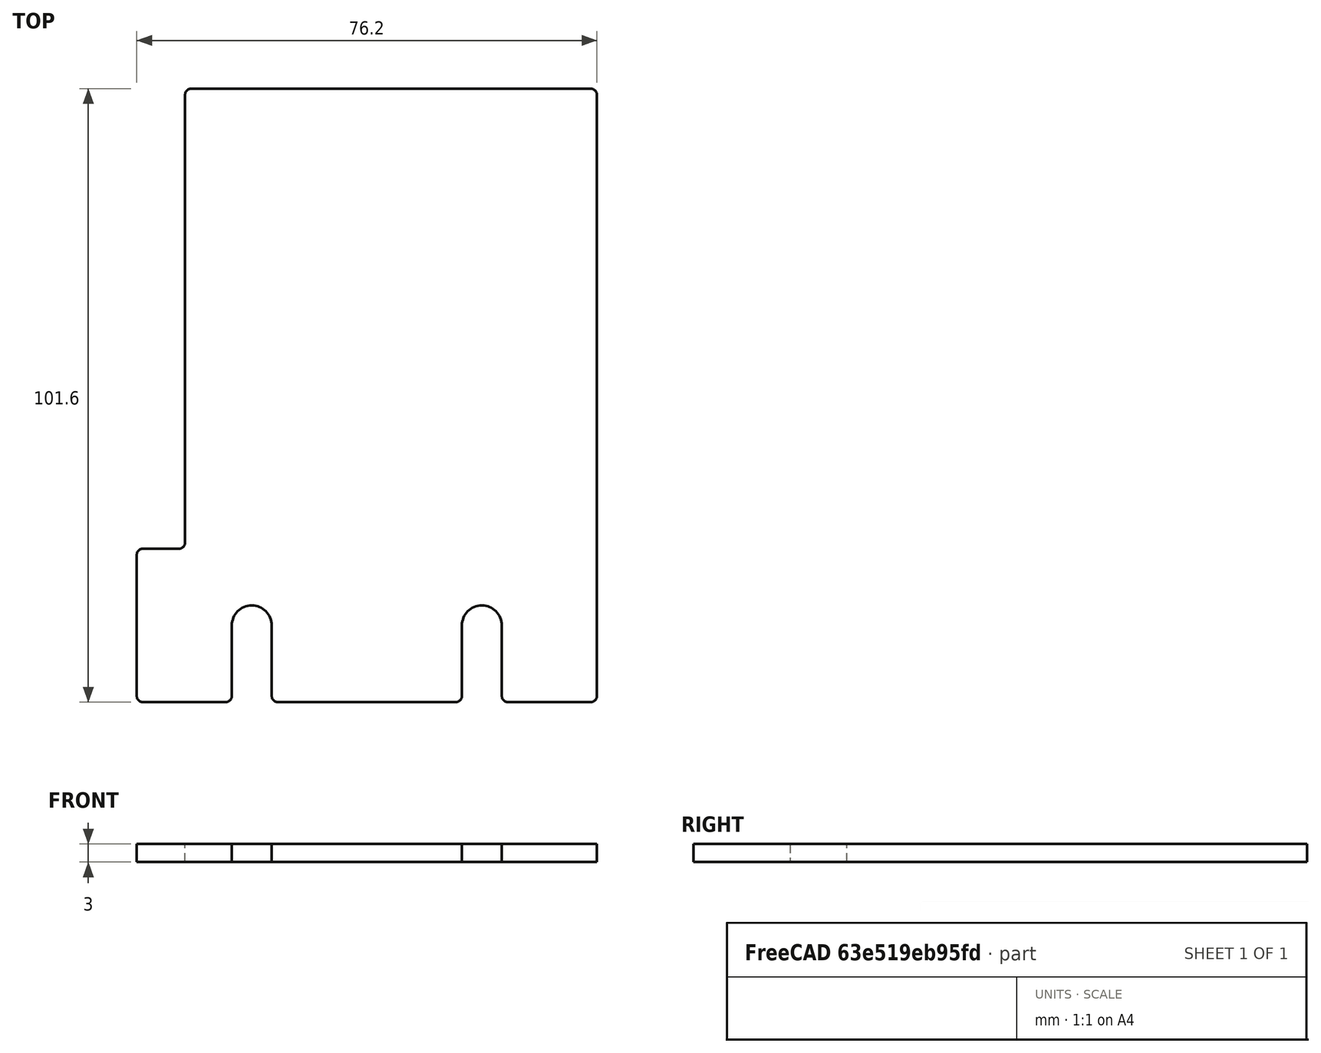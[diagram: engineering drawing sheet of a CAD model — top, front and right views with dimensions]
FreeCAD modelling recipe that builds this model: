
FCSTD DOCUMENT  (FreeCAD 0.21R33675 (Git))
Label: plain_wall_3in_with_door_gap
License: All rights reserved
LicenseURL: http://en.wikipedia.org/wiki/All_rights_reserved
objects: Sketcher::SketchObject×1, Spreadsheet::Sheet×1, PartDesign::Pad×1, PartDesign::Body×1
note: 4 computed .brp shape members not serialized (recipe doc carries the construction recipe); baked Part::Feature solids carry a one-line shape summary decoded from their .brp

FEATURE [Sketcher::SketchObject] Sketch
  FullyConstrained = true
  MapMode = 5
  Support = -> [XY_Plane]
  expr: Constraints[15] = Spreadsheet.FilletRadius
  expr: Constraints[17] = Spreadsheet.Height
  expr: Constraints[22] = Spreadsheet.MountHoleDistanceFromBottom
  expr: Constraints[24] = Spreadsheet.MountHoleDiameter
  expr: Constraints[36] = Spreadsheet.MountHoleSideMargin
  expr: Constraints[45] = Spreadsheet.Length
  expr: Constraints[50] = Spreadsheet.DoorGap
  expr: Constraints[51] = Spreadsheet.BeamHeight
  sketch-geometry (34):
    g0: ArcOfCircle CenterX=-29.1 CenterY=49.8 CenterZ=0 NormalX=0 NormalY=0 NormalZ=1 AngleXU=0 Radius=1 StartAngle=1.5708 EndAngle=3.14159
    g1: LineSegment StartX=-29.1 StartY=50.8 StartZ=0 EndX=37.1 EndY=50.8 EndZ=0
    g2: ArcOfCircle CenterX=37.1 CenterY=49.8 CenterZ=0 NormalX=0 NormalY=0 NormalZ=1 AngleXU=0 Radius=1 StartAngle=3.911e-13 EndAngle=1.5708
    g3: LineSegment StartX=38.1 StartY=49.8 StartZ=0 EndX=38.1 EndY=-49.8 EndZ=0
    g4: ArcOfCircle CenterX=37.1 CenterY=-49.8 CenterZ=0 NormalX=0 NormalY=0 NormalZ=1 AngleXU=0 Radius=1 StartAngle=4.71239 EndAngle=6.28319
    g5: LineSegment StartX=37.1 StartY=-50.8 StartZ=0 EndX=-37.1 EndY=-50.8 EndZ=0
    g6: ArcOfCircle CenterX=-37.1 CenterY=-49.8 CenterZ=0 NormalX=0 NormalY=0 NormalZ=1 AngleXU=0 Radius=1 StartAngle=3.14159 EndAngle=4.71239
    g7: GeomPoint X=-38.1 Y=50.8 Z=0
    g8: GeomPoint X=38.1 Y=-50.8 Z=0
    g9: LineSegment StartX=-19.05 StartY=-38.1 StartZ=0 EndX=19.05 EndY=-38.1 EndZ=0
    g10: LineSegment StartX=0 StartY=-50.8 StartZ=0 EndX=0 EndY=-38.1 EndZ=0
    g11: Circle CenterX=-19.05 CenterY=-38.1 CenterZ=0 NormalX=0 NormalY=0 NormalZ=1 AngleXU=0 Radius=3.302
    g12: Circle CenterX=19.05 CenterY=-38.1 CenterZ=0 NormalX=0 NormalY=0 NormalZ=1 AngleXU=0 Radius=3.302
    g13: LineSegment StartX=0 StartY=-38.1 StartZ=0 EndX=0 EndY=-50.8 EndZ=0
    g14: LineSegment StartX=-19.05 StartY=-38.1 StartZ=0 EndX=-38.1 EndY=-38.1 EndZ=0
    g15: LineSegment StartX=19.05 StartY=-38.1 StartZ=0 EndX=38.1 EndY=-38.1 EndZ=0
    g16: LineSegment StartX=-38.1 StartY=-49.8 StartZ=0 EndX=-38.1 EndY=-26.4 EndZ=0
    g17: ArcOfCircle CenterX=-37.1 CenterY=-26.4 CenterZ=0 NormalX=0 NormalY=0 NormalZ=1 AngleXU=0 Radius=1 StartAngle=1.5708 EndAngle=3.14159
    g18: LineSegment StartX=-37.1 StartY=-25.4 StartZ=0 EndX=-31.1 EndY=-25.4 EndZ=0
    g19: LineSegment StartX=-30.1 StartY=49.8 StartZ=0 EndX=-30.1 EndY=-24.4 EndZ=0
    g20: ArcOfCircle CenterX=-31.1 CenterY=-24.4 CenterZ=0 NormalX=0 NormalY=0 NormalZ=1 AngleXU=0 Radius=1 StartAngle=4.71239 EndAngle=6.28319
    g21: ArcOfCircle CenterX=-19.05 CenterY=-38.1 CenterZ=0 NormalX=0 NormalY=0 NormalZ=1 AngleXU=0 Radius=3.302 StartAngle=0 EndAngle=3.14159
    g22: LineSegment StartX=-22.352 StartY=-38.1 StartZ=0 EndX=-22.352 EndY=-49.8 EndZ=0
    g23: LineSegment StartX=-15.748 StartY=-38.1 StartZ=0 EndX=-15.748 EndY=-49.8 EndZ=0
    g24: ArcOfCircle CenterX=-23.352 CenterY=-49.8 CenterZ=0 NormalX=0 NormalY=0 NormalZ=1 AngleXU=0 Radius=1 StartAngle=4.71239 EndAngle=6.28319
    g25: ArcOfCircle CenterX=-14.748 CenterY=-49.8 CenterZ=0 NormalX=0 NormalY=0 NormalZ=1 AngleXU=0 Radius=1 StartAngle=3.14159 EndAngle=4.71239
    g26: ArcOfCircle CenterX=19.05 CenterY=-38.1 CenterZ=0 NormalX=0 NormalY=0 NormalZ=1 AngleXU=0 Radius=3.302 StartAngle=-9e-16 EndAngle=3.14159
    g27: LineSegment StartX=15.748 StartY=-38.1 StartZ=0 EndX=15.748 EndY=-49.8 EndZ=0
    g28: LineSegment StartX=22.352 StartY=-38.1 StartZ=0 EndX=22.352 EndY=-49.8 EndZ=0
    g29: ArcOfCircle CenterX=14.748 CenterY=-49.8 CenterZ=0 NormalX=0 NormalY=0 NormalZ=1 AngleXU=0 Radius=1 StartAngle=4.71239 EndAngle=6.28319
    g30: ArcOfCircle CenterX=23.352 CenterY=-49.8 CenterZ=0 NormalX=0 NormalY=0 NormalZ=1 AngleXU=0 Radius=1 StartAngle=3.14159 EndAngle=4.71239
    g31: LineSegment StartX=-37.1 StartY=-50.8 StartZ=0 EndX=-23.352 EndY=-50.8 EndZ=0
    g32: LineSegment StartX=-14.748 StartY=-50.8 StartZ=0 EndX=14.748 EndY=-50.8 EndZ=0
    g33: LineSegment StartX=23.352 StartY=-50.8 StartZ=0 EndX=37.1 EndY=-50.8 EndZ=0
  constraints (87):
    c: Tangent(g0,g1) = 1.5708
    c: Tangent(g1,g2) = 1.5708
    c: Tangent(g2,g3) = 1.5708
    c: Tangent(g3,g4) = 1.5708
    c: Tangent(g4,g5) = 1.5708
    c: Tangent(g5,g6) = 1.5708
    c: Horizontal(g1)
    c: Horizontal(g5)
    c: Vertical(g3)
    c: Equal(g0,g2)
    c: Equal(g2,g4)
    c: Equal(g4,g6)
    c: PointOnObject(g7,g1)
    c: PointOnObject(g8,g3)
    c: PointOnObject(g8,g5)
    c: Radius(g2) = 1
    c: Symmetric(g7,g8,g-1)
    c: DistanceY(g4,g1) = 101.6
    c: Horizontal(g9)
    c: Vertical(g10)
    c: PointOnObject(g10,g5)
    c: PointOnObject(g10,g-2)
    c: DistanceY(g10,g10) = 12.7
    c: Coincident(g12,g9)
    c: Diameter(g12) = 6.604
    c: Equal(g11,g12)
    c: Coincident(g11,g9)
    c: PointOnObject(g13,g9)
    c: Vertical(g13)
    c: Coincident(g13,g10)
    c: Coincident(g14,g11)
    c: Horizontal(g14)
    c: Coincident(g15,g12)
    c: PointOnObject(g15,g3)
    c: Horizontal(g15)
    c: Equal(g15,g14)
    c: DistanceX(g14,g14) = 19.05
    c: Vertical(g16)
    c: PointOnObject(g14,g16)
    c: Tangent(g17,g16) = 1.5708
    c: Horizontal(g18)
    c: Tangent(g18,g17) = 1.5708
    c: Equal(g17,g6)
    c: Vertical(g19)
    c: Tangent(g0,g19) = -1.5708
    c: DistanceX(g6,g3) = 76.2
    c: Symmetric(g11,g12,g10)
    c: Tangent(g20,g18) = -1.5708
    c: Tangent(g20,g19) = 1.5708
    c: Equal(g20,g17)
    c: DistanceX(g16,g19) = 8
    c: DistanceY(g5,g17) = 25.4
    c: Tangent(g16,g6) = 1.5708
    c: Coincident(g21,g9)
    c: PointOnObject(g21,g11)
    c: PointOnObject(g21,g14)
    c: PointOnObject(g21,g9)
    c: Vertical(g22)
    c: Vertical(g23)
    c: Equal(g22,g23)
    c: Coincident(g22,g21)
    c: Coincident(g23,g21)
    c: Tangent(g24,g22) = 1.5708
    c: Tangent(g24,g5) = 1.5708
    c: Tangent(g25,g23) = -1.5708
    c: Tangent(g25,g5) = 1.5708
    c: Equal(g6,g24)
    c: Coincident(g26,g9)
    c: PointOnObject(g26,g9)
    c: PointOnObject(g26,g15)
    c: PointOnObject(g26,g12)
    c: Vertical(g27)
    c: Vertical(g28)
    c: Equal(g27,g28)
    c: Coincident(g27,g26)
    c: Coincident(g28,g26)
    c: Tangent(g30,g28) = -1.5708
    c: Tangent(g30,g5) = 1.5708
    c: Tangent(g29,g27) = 1.5708
    c: Tangent(g29,g5) = 1.5708
    c: Equal(g30,g4)
    c: Coincident(g31,g6)
    c: Coincident(g24,g31)
    c: Coincident(g32,g25)
    c: Coincident(g29,g32)
    c: Coincident(g33,g30)
    c: Coincident(g4,g33)
FEATURE [Spreadsheet::Sheet] Spreadsheet
  cells = A2='Parameters; A3='Height; B3(Height)==4 in; A4='Length; B4(Length)==3 in; A5='Thickness; B5(Thickness)==3 mm; A6='FilletRadius; B6(FilletRadius)==1 mm; A7='MountHoleDiameter; B7(MountHoleDiameter)==0.26 in; A8='MountHoleDistanceFromBottom; B8(MountHoleDistanceFromBottom)==0.5 in; A9='MountHoleSideMargin; B9(MountHoleSideMargin)==0.75 in; A10='BeamHeight; B10(BeamHeight)==1 in; A11='DoorGap; B11(DoorGap)==8 mm
FEATURE [PartDesign::Pad] Pad
  Direction = (0,0,1)
  Length = 3
  Length2 = 10
  Profile = -> Sketch
  ReferenceAxis = -> Sketch [N_Axis]
  Type = 0
  expr: Length = Spreadsheet.Thickness
FEATURE [PartDesign::Body] Body
  Group = -> [Sketch,Pad]
  Origin = -> Origin
  Tip = -> Pad
